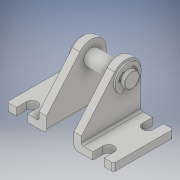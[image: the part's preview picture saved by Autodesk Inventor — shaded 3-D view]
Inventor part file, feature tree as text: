
AUTODESK INVENTOR PART (.ipt)
format: ipt  version: 2017 (Build 210142000, 142)  size: 245,760 bytes
history: native  units: in
note: dims shown in document units (in); Inventor stores cm internally (conversion verified against a paired STEP export)
features: other x2, fillet x2, revolve x1, mirror x1
ambient origin geometry x8: Origin, YZ Plane, XZ Plane, XY Plane, X Axis, Y Axis, Z Axis, Center Point
bodies: Solid1 (feature_tree), Solid2 (feature_tree), Solid3 (feature_tree), Solid4 (feature_tree), Solid5 (feature_tree)
feature tree (6):
  other  "4952K678_SENSOR-READY ROUND BODY AIR CYLINDER1"
  fillet  "Fillet2"  [1 undecoded]
  fillet  "Fillet4"  [1 undecoded]
  revolve  "Revolve1"  [1 undecoded]
  other  "Boss-Extrude5"
  mirror  "Mirror1"
note: 3 required parameter values undecoded (feature->parameter linkage not recoverable at this tier; creation-order binding heuristic only, values carry confidence <= 0.55)
